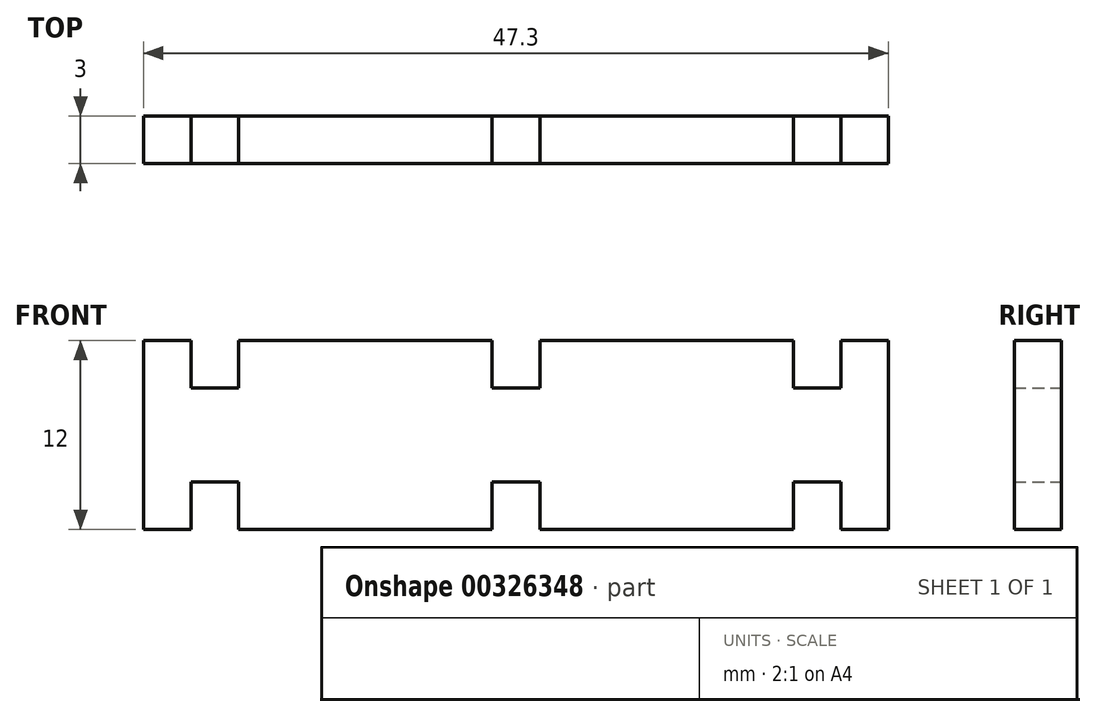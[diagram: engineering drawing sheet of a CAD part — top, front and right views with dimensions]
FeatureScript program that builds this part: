
annotation { "Feature Type Name" : "Feature", "Feature Type Description" : "" }
export const myFeature = defineFeature(function(context is Context, id is Id, definition is map)
    precondition{}
    {
        {
            var Q0;
            Q0=qCreatedBy(makeId("Front.planeOp"),FACE);
            var sketch = newSketch(context, id + "F0", { "sketchPlane" : qUnion([Q0])});
            skPoint(sketch, "E0", {"position": v(-20.65, 0) * mm});
            skPoint(sketch, "E1", {"position": v(-20.65, 3.02) * mm});
            skPoint(sketch, "E2", {"position": v(-17.61, 3.02) * mm});
            skPoint(sketch, "E3", {"position": v(20.65, 0) * mm});
            skPoint(sketch, "E4", {"position": v(20.65, 3.02) * mm});
            skPoint(sketch, "E5", {"position": v(17.6, 3.02) * mm});
            skPoint(sketch, "E6", {"position": v(17.6, 0) * mm});
            skLineSegment(sketch, "E7", {"start": v(-20.65, 0) * mm, "end": v(-20.65, 3.02) * mm});
            skLineSegment(sketch, "E8", {"start": v(-17.61, 3.02) * mm, "end": v(-20.65, 3.02) * mm});
            skLineSegment(sketch, "E9", {"start": v(-17.61, 0) * mm, "end": v(-17.61, 3.02) * mm});
            skLineSegment(sketch, "E10", {"start": v(17.6, 0) * mm, "end": v(17.6, 3.02) * mm});
            skLineSegment(sketch, "E11", {"start": v(20.65, 3.02) * mm, "end": v(17.6, 3.02) * mm});
            skLineSegment(sketch, "E12", {"start": v(20.65, 0) * mm, "end": v(20.65, 3.02) * mm});
            skLineSegment(sketch, "E13.trimOffspring", {"start": v(20.65, 0) * mm, "end": v(23.65, 0) * mm});
            skLineSegment(sketch, "E14.trimOffspring", {"start": v(-20.65, 0) * mm, "end": v(-23.65, 0) * mm});
            skLineSegment(sketch, "E15", {"start": v(-23.65, 12) * mm, "end": v(-20.65, 12) * mm});
            skLineSegment(sketch, "E16", {"start": v(-20.65, 12) * mm, "end": v(-20.65, 8.98) * mm});
            skLineSegment(sketch, "E17", {"start": v(-20.65, 8.98) * mm, "end": v(-17.6, 8.98) * mm});
            skLineSegment(sketch, "E18", {"start": v(-17.6, 8.98) * mm, "end": v(-17.6, 12) * mm});
            skLineSegment(sketch, "E19", {"start": v(23.65, 12) * mm, "end": v(20.65, 12) * mm});
            skLineSegment(sketch, "E20", {"start": v(20.65, 12) * mm, "end": v(20.65, 8.98) * mm});
            skLineSegment(sketch, "E21", {"start": v(20.65, 8.98) * mm, "end": v(17.6, 8.98) * mm});
            skLineSegment(sketch, "E22", {"start": v(17.6, 8.98) * mm, "end": v(17.6, 12) * mm});
            skLineSegment(sketch, "E23", {"start": v(17.6, 12) * mm, "end": v(1.52, 12) * mm});
            skLineSegment(sketch, "E24", {"start": v(23.65, 12) * mm, "end": v(23.65, 0) * mm});
            skLineSegment(sketch, "E25", {"start": v(-23.65, 12) * mm, "end": v(-23.65, 0) * mm});
            skLineSegment(sketch, "E26", {"start": v(-17.61, 0) * mm, "end": v(-1.52, 0) * mm});
            skLineSegment(sketch, "E27", {"start": v(-1.52, 12) * mm, "end": v(-1.52, 8.98) * mm});
            skLineSegment(sketch, "E28", {"start": v(1.52, 12) * mm, "end": v(1.52, 8.98) * mm});
            skLineSegment(sketch, "E29", {"start": v(-1.52, 0) * mm, "end": v(-1.52, 3.02) * mm});
            skLineSegment(sketch, "E30", {"start": v(1.52, 0) * mm, "end": v(1.52, 3.02) * mm});
            skLineSegment(sketch, "E31", {"start": v(-1.52, 3.02) * mm, "end": v(1.52, 3.02) * mm});
            skLineSegment(sketch, "E32", {"start": v(-1.52, 8.98) * mm, "end": v(1.52, 8.98) * mm});
            skLineSegment(sketch, "E33.trimOffspring", {"start": v(-1.52, 12) * mm, "end": v(-17.6, 12) * mm});
            skLineSegment(sketch, "E34.trimOffspring", {"start": v(1.52, 0) * mm, "end": v(17.6, 0) * mm});
            skSolve(sketch);
        }
        {
            var Q0;
            Q0=makeQuery(id+"F0.imprint","IMPRINT",FACE,{"disambiguationData":[TD([[makeQuery(id+"F0.imprint","IMPRINT",EDGE,{"derivedFrom":sQuery(id+"F0.wireOp",EDGE,"E7")}),1.0]])]});
            extrude(context, id + "F1", {"entities" : qUnion([Q0]), "depth" : 3 * mm});
        }
    });
